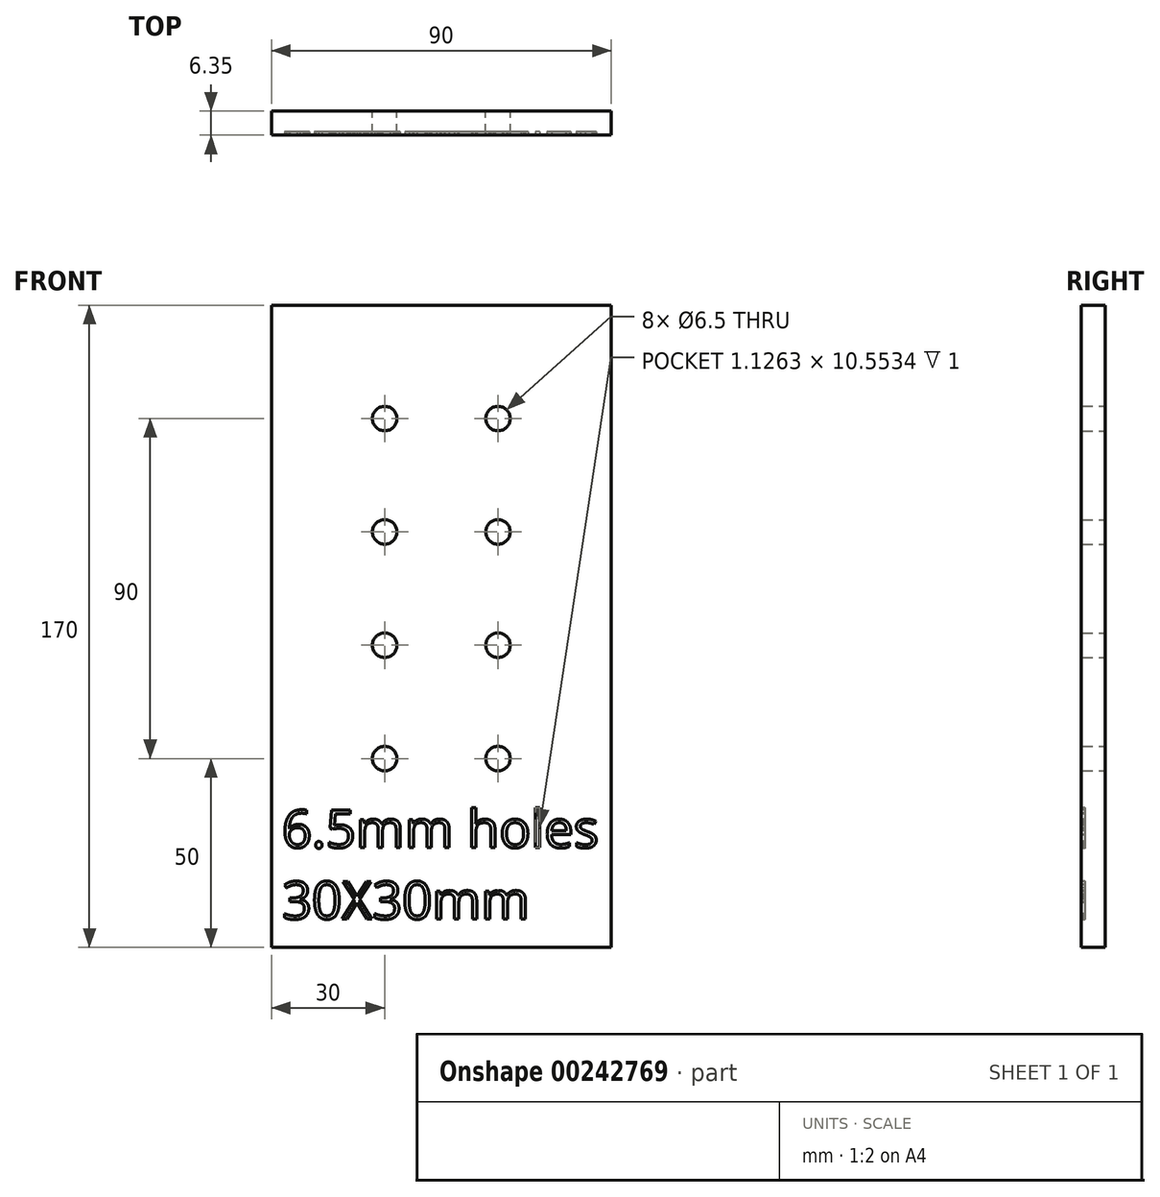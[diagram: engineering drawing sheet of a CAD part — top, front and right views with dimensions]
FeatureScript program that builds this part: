
annotation { "Feature Type Name" : "Feature", "Feature Type Description" : "" }
export const myFeature = defineFeature(function(context is Context, id is Id, definition is map)
    precondition{}
    {
        {
            var Q0;
            Q0=qCreatedBy(makeId("Front.planeOp"),FACE);
            var sketch = newSketch(context, id + "F0", { "sketchPlane" : qUnion([Q0])});
            skLineSegment(sketch, "E0.bottom", {"start": v(-45, 85) * mm, "end": v(45, 85) * mm});
            skLineSegment(sketch, "E0.top", {"start": v(-45, -85) * mm, "end": v(45, -85) * mm});
            skLineSegment(sketch, "E0.left", {"start": v(-45, 85) * mm, "end": v(-45, -85) * mm});
            skLineSegment(sketch, "E1", {"start": v(-15, 85) * mm, "end": v(-15, 55) * mm, "construction": true});
            skLineSegment(sketch, "E2", {"start": v(-15, 55) * mm, "end": v(-45, 55) * mm, "construction": true});
            skCircle(sketch, "E3", {"center": v(-15, 55) * mm, "radius": 3.25 * mm});
            skLineSegment(sketch, "E4", {"start": v(45, 85) * mm, "end": v(45, -85) * mm});
            skLineSegment(sketch, "E5", {"start": v(-48.1, 0) * mm, "end": v(43.52, 0) * mm, "construction": true});
            skLineSegment(sketch, "E6", {"start": v(0, 55.66) * mm, "end": v(0, -47.1) * mm, "construction": true});
            skCircle(sketch, "E7.0.1.0", {"center": v(-15, 25) * mm, "radius": 3.25 * mm});
            skCircle(sketch, "E7.1.0.0", {"center": v(15, 55) * mm, "radius": 3.25 * mm});
            skCircle(sketch, "E7.1.1.0", {"center": v(15, 25) * mm, "radius": 3.25 * mm});
            skLineSegment(sketch, "E7.direction1", {"start": v(-15, 55) * mm, "end": v(15, 55) * mm, "construction": true});
            skLineSegment(sketch, "E7.direction2", {"start": v(-15, 55) * mm, "end": v(-15, 25) * mm, "construction": true});
            skCircle(sketch, "E8", {"center": v(-415, 250) * mm, "radius": 1.5 * mm});
            skCircle(sketch, "E9.0.0.2", {"center": v(-15, -5) * mm, "radius": 3.25 * mm});
            skCircle(sketch, "E9.0.0.3", {"center": v(-15, -35) * mm, "radius": 3.25 * mm});
            skCircle(sketch, "E9.0.1.2", {"center": v(15, -5) * mm, "radius": 3.25 * mm});
            skCircle(sketch, "E9.0.1.3", {"center": v(15, -35) * mm, "radius": 3.25 * mm});
            skSolve(sketch);
        }
        {
            var Q0;
            Q0=qSketchRegion(id+"F0",true);
            extrude(context, id + "F1", {"entities" : qUnion([Q0]), "depth" : 6.35 * mm});
        }
        {
            var Q0;
            Q0=makeQuery(id+"F1.opExtrude","SWEPT_BODY",BODY,{"disambiguationData":[OSD([sQuery(id+"F0.wireOp",EDGE,"E8")])]});
            deleteBodies(context, id + "F2", {"entities" : qUnion([Q0])});
        }
        {
            var Q0;
            Q0=makeQuery(id+"F1.opExtrude","CAP_FACE",FACE,{"disambiguationData":[OSD([sQuery(id+"F0.wireOp",EDGE,"E0.bottom"),sQuery(id+"F0.wireOp",EDGE,"E0.top"),sQuery(id+"F0.wireOp",EDGE,"E0.left"),sQuery(id+"F0.wireOp",EDGE,"E3"),sQuery(id+"F0.wireOp",EDGE,"E4"),sQuery(id+"F0.wireOp",EDGE,"E7.0.1.0"),sQuery(id+"F0.wireOp",EDGE,"E7.1.0.0"),sQuery(id+"F0.wireOp",EDGE,"E7.1.1.0"),sQuery(id+"F0.wireOp",EDGE,"E9.0.0.2"),sQuery(id+"F0.wireOp",EDGE,"E9.0.0.3"),sQuery(id+"F0.wireOp",EDGE,"E9.0.1.2"),sQuery(id+"F0.wireOp",EDGE,"E9.0.1.3")])],"isStart":false});
            var sketch = newSketch(context, id + "F3", { "sketchPlane" : qUnion([Q0])});
            skText(sketch, "E10", { "text": "6.5mm holes\n30X30mm", "fontName": "OpenSans-Regular.ttf"});
            const initialGuessF3  = {"E10": [-0.04222, -0.05858, 1, 0, 0.01]};
            skSetInitialGuess(sketch, initialGuessF3);
            skSolve(sketch);
        }
        {
            var Q0;
            Q0=qSketchRegion(id+"F3",true);
            extrude(context, id + "F4", {"entities" : qUnion([Q0]), "operationType" : NewBodyOperationType.REMOVE, "oppositeDirection" : true, "depth" : 1 * mm});
        }
    });
